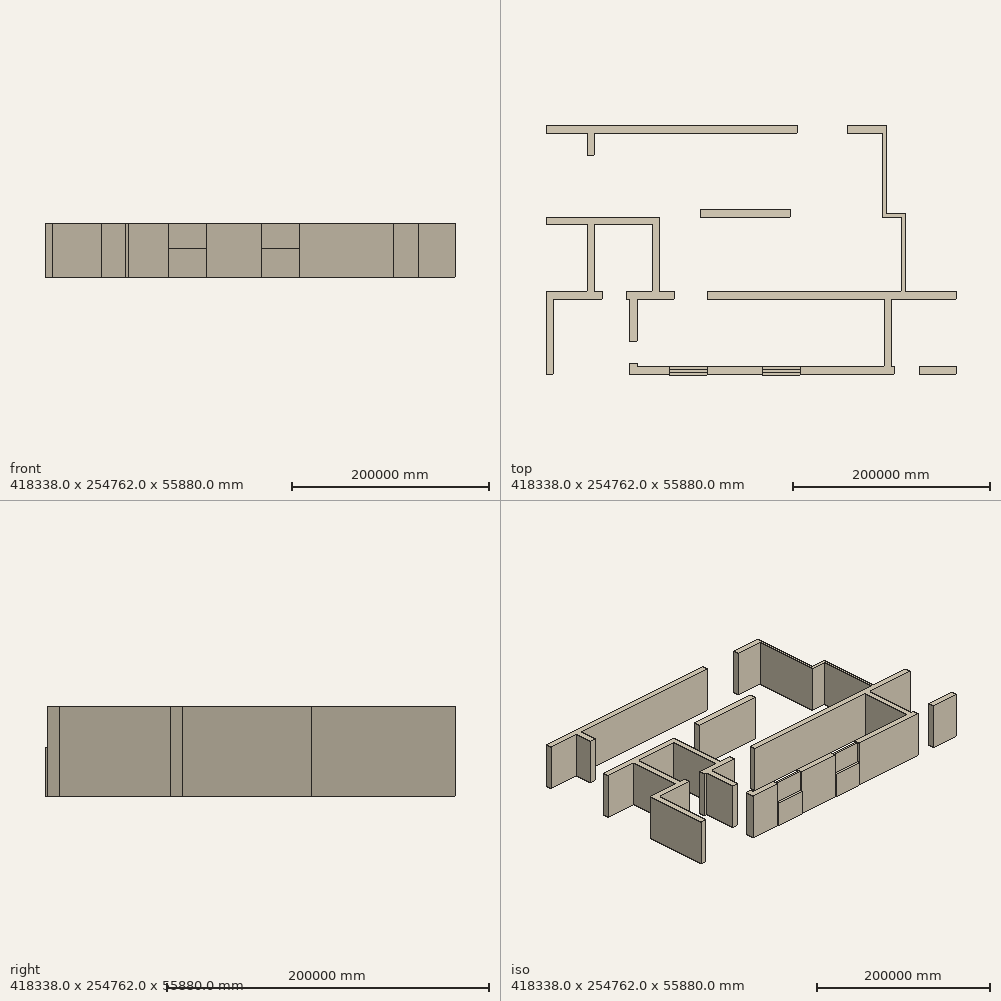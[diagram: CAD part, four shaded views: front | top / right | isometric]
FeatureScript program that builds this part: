
annotation { "Feature Type Name" : "Feature", "Feature Type Description" : "" }
export const myFeature = defineFeature(function(context is Context, id is Id, definition is map)
    precondition{}
    {
        {
            var Q0;
            Q0=qCreatedBy(makeId("Top.planeOp"),FACE);
            var sketch = newSketch(context, id + "F0", { "sketchPlane" : qUnion([Q0])});
            skLineSegment(sketch, "E0", {"start": v(0, 0) * mm, "end": v(115316, 0) * mm});
            skLineSegment(sketch, "E1", {"start": v(115316, 0) * mm, "end": v(115316, -76200) * mm});
            skLineSegment(sketch, "E2", {"start": v(115316, -76200) * mm, "end": v(130810, -76200) * mm});
            skLineSegment(sketch, "E3", {"start": v(130810, -76200) * mm, "end": v(130810, -83820) * mm});
            skLineSegment(sketch, "E4", {"start": v(130810, -83820) * mm, "end": v(92710, -83820) * mm});
            skLineSegment(sketch, "E5", {"start": v(92710, -83820) * mm, "end": v(92710, -127000) * mm});
            skLineSegment(sketch, "E6", {"start": v(92710, -127000) * mm, "end": v(85090, -127000) * mm});
            skLineSegment(sketch, "E7", {"start": v(85090, -127000) * mm, "end": v(85090, -83820) * mm});
            skLineSegment(sketch, "E8", {"start": v(85090, -83820) * mm, "end": v(81280, -83820) * mm});
            skLineSegment(sketch, "E9", {"start": v(81280, -83820) * mm, "end": v(81280, -76200) * mm});
            skLineSegment(sketch, "E10", {"start": v(81280, -76200) * mm, "end": v(107696, -76200) * mm});
            skLineSegment(sketch, "E11", {"start": v(107696, -76200) * mm, "end": v(107696, -7620) * mm});
            skLineSegment(sketch, "E12", {"start": v(107696, -7620) * mm, "end": v(49276, -7620) * mm});
            skLineSegment(sketch, "E13", {"start": v(49276, -7620) * mm, "end": v(49276, -76200) * mm});
            skLineSegment(sketch, "E14", {"start": v(49276, -76200) * mm, "end": v(56896, -76200) * mm});
            skLineSegment(sketch, "E15", {"start": v(56896, -76200) * mm, "end": v(56896, -83820) * mm});
            skLineSegment(sketch, "E16", {"start": v(56896, -83820) * mm, "end": v(7620, -83820) * mm});
            skLineSegment(sketch, "E17", {"start": v(7620, -83820) * mm, "end": v(7620, -160020) * mm});
            skLineSegment(sketch, "E18", {"start": v(7620, -160020) * mm, "end": v(0, -160020) * mm});
            skLineSegment(sketch, "E19", {"start": v(0, -160020) * mm, "end": v(0, -76200) * mm});
            skLineSegment(sketch, "E20", {"start": v(0, -76200) * mm, "end": v(41656, -76200) * mm});
            skLineSegment(sketch, "E21", {"start": v(41656, -76200) * mm, "end": v(41656, -7620) * mm});
            skLineSegment(sketch, "E22", {"start": v(41656, -7620) * mm, "end": v(0, -7620) * mm});
            skLineSegment(sketch, "E23", {"start": v(0, -7620) * mm, "end": v(0, 0) * mm});
            skLineSegment(sketch, "E24", {"start": v(164338, -83820) * mm, "end": v(164338, -76200) * mm});
            skLineSegment(sketch, "E25", {"start": v(164338, -76200) * mm, "end": v(362458, -76200) * mm});
            skLineSegment(sketch, "E26", {"start": v(418338, -76200) * mm, "end": v(418338, -83820) * mm});
            skLineSegment(sketch, "E27", {"start": v(418338, -83820) * mm, "end": v(352298, -83820) * mm});
            skLineSegment(sketch, "E28", {"start": v(352298, -83820) * mm, "end": v(352298, -152400) * mm});
            skLineSegment(sketch, "E29", {"start": v(352298, -152400) * mm, "end": v(355346, -152400) * mm});
            skLineSegment(sketch, "E30", {"start": v(355346, -152400) * mm, "end": v(355346, -160020) * mm});
            skLineSegment(sketch, "E31", {"start": v(355346, -160020) * mm, "end": v(258826, -160020) * mm});
            skLineSegment(sketch, "E32", {"start": v(258826, -160020) * mm, "end": v(258826, -152400) * mm});
            skLineSegment(sketch, "E33", {"start": v(258826, -152400) * mm, "end": v(344678, -152400) * mm});
            skLineSegment(sketch, "E34", {"start": v(344678, -152400) * mm, "end": v(344678, -83820) * mm});
            skLineSegment(sketch, "E35", {"start": v(344678, -83820) * mm, "end": v(164338, -83820) * mm});
            skLineSegment(sketch, "E36", {"start": v(380746, -152400) * mm, "end": v(380746, -160020) * mm});
            skLineSegment(sketch, "E37", {"start": v(380746, -160020) * mm, "end": v(418338, -160020) * mm});
            skLineSegment(sketch, "E38", {"start": v(418338, -160020) * mm, "end": v(418338, -152400) * mm});
            skLineSegment(sketch, "E39", {"start": v(418338, -152400) * mm, "end": v(380746, -152400) * mm});
            skLineSegment(sketch, "E40", {"start": v(85090, -160020) * mm, "end": v(125730, -160020) * mm});
            skLineSegment(sketch, "E41", {"start": v(125730, -160020) * mm, "end": v(125730, -152400) * mm});
            skLineSegment(sketch, "E42", {"start": v(125730, -152400) * mm, "end": v(92710, -152400) * mm});
            skLineSegment(sketch, "E43", {"start": v(92710, -152400) * mm, "end": v(92710, -148844) * mm});
            skLineSegment(sketch, "E44", {"start": v(92710, -148844) * mm, "end": v(85090, -148844) * mm});
            skLineSegment(sketch, "E45", {"start": v(85090, -148844) * mm, "end": v(85090, -160020) * mm});
            skLineSegment(sketch, "E46", {"start": v(164338, -152400) * mm, "end": v(220218, -152400) * mm});
            skLineSegment(sketch, "E47", {"start": v(220218, -152400) * mm, "end": v(220218, -160020) * mm});
            skLineSegment(sketch, "E48", {"start": v(220218, -160020) * mm, "end": v(164338, -160020) * mm});
            skLineSegment(sketch, "E49", {"start": v(164338, -160020) * mm, "end": v(164338, -152400) * mm});
            skLineSegment(sketch, "E50", {"start": v(125730, -152400) * mm, "end": v(164338, -152400) * mm});
            skLineSegment(sketch, "E51", {"start": v(125730, -160020) * mm, "end": v(125730, -161290) * mm});
            skLineSegment(sketch, "E52", {"start": v(125730, -161290) * mm, "end": v(164338, -161290) * mm});
            skLineSegment(sketch, "E53", {"start": v(164338, -161290) * mm, "end": v(164338, -160020) * mm});
            skLineSegment(sketch, "E54", {"start": v(125730, -155575) * mm, "end": v(164338, -155575) * mm});
            skLineSegment(sketch, "E55", {"start": v(164338, -155575) * mm, "end": v(164338, -158115) * mm});
            skLineSegment(sketch, "E56", {"start": v(164338, -158115) * mm, "end": v(125730, -158115) * mm});
            skLineSegment(sketch, "E57", {"start": v(125730, -158115) * mm, "end": v(125730, -155575) * mm});
            skLineSegment(sketch, "E58", {"start": v(220218, -152400) * mm, "end": v(258826, -152400) * mm});
            skLineSegment(sketch, "E59", {"start": v(258826, -160020) * mm, "end": v(258826, -161290) * mm});
            skLineSegment(sketch, "E60", {"start": v(258826, -161290) * mm, "end": v(220218, -161290) * mm});
            skLineSegment(sketch, "E61", {"start": v(220218, -161290) * mm, "end": v(220218, -160020) * mm});
            skLineSegment(sketch, "E62", {"start": v(220218, -155575) * mm, "end": v(258826, -155575) * mm});
            skLineSegment(sketch, "E63", {"start": v(258826, -155575) * mm, "end": v(258826, -158115) * mm});
            skLineSegment(sketch, "E64", {"start": v(258826, -158115) * mm, "end": v(220218, -158115) * mm});
            skLineSegment(sketch, "E65", {"start": v(220218, -158115) * mm, "end": v(220218, -155575) * mm});
            skLineSegment(sketch, "E66", {"start": v(362458, -76200) * mm, "end": v(362458, 0) * mm});
            skLineSegment(sketch, "E67", {"start": v(362458, 0) * mm, "end": v(342646, 0) * mm});
            skLineSegment(sketch, "E68", {"start": v(342646, 0) * mm, "end": v(342646, 85852) * mm});
            skLineSegment(sketch, "E69", {"start": v(342646, 85852) * mm, "end": v(307086, 85852) * mm});
            skLineSegment(sketch, "E70", {"start": v(307086, 85852) * mm, "end": v(307086, 93472) * mm});
            skLineSegment(sketch, "E71", {"start": v(307086, 93472) * mm, "end": v(346456, 93472) * mm});
            skLineSegment(sketch, "E72", {"start": v(346456, 93472) * mm, "end": v(346456, 3810) * mm});
            skLineSegment(sketch, "E73", {"start": v(346456, 3810) * mm, "end": v(366268, 3810) * mm});
            skLineSegment(sketch, "E74", {"start": v(366268, 3810) * mm, "end": v(366268, -76200) * mm});
            skLineSegment(sketch, "E75.trimOffspring", {"start": v(366268, -76200) * mm, "end": v(418338, -76200) * mm});
            skLineSegment(sketch, "E76", {"start": v(248666, 0) * mm, "end": v(157226, 0) * mm});
            skLineSegment(sketch, "E77", {"start": v(157226, 0) * mm, "end": v(157226, 7620) * mm});
            skLineSegment(sketch, "E78", {"start": v(157226, 7620) * mm, "end": v(248666, 7620) * mm});
            skLineSegment(sketch, "E79", {"start": v(248666, 7620) * mm, "end": v(248666, 0) * mm});
            skLineSegment(sketch, "E80", {"start": v(256286, 85852) * mm, "end": v(49276, 85852) * mm});
            skLineSegment(sketch, "E81", {"start": v(49276, 85852) * mm, "end": v(49276, 62992) * mm});
            skLineSegment(sketch, "E82", {"start": v(49276, 62992) * mm, "end": v(41656, 62992) * mm});
            skLineSegment(sketch, "E83", {"start": v(41656, 62992) * mm, "end": v(41656, 85852) * mm});
            skLineSegment(sketch, "E84", {"start": v(41656, 85852) * mm, "end": v(0, 85852) * mm});
            skLineSegment(sketch, "E85", {"start": v(0, 85852) * mm, "end": v(0, 93472) * mm});
            skLineSegment(sketch, "E86", {"start": v(0, 93472) * mm, "end": v(256286, 93472) * mm});
            skLineSegment(sketch, "E87", {"start": v(256286, 93472) * mm, "end": v(256286, 85852) * mm});
            skSolve(sketch);
        }
        {
            var Q0;
            Q0=makeQuery(id+"F0.imprint","IMPRINT",FACE,{"disambiguationData":[TD([[makeQuery(id+"F0.imprint","IMPRINT",EDGE,{"derivedFrom":sQuery(id+"F0.wireOp",EDGE,"E0")}),-1.0]])]});
            var Q1;
            Q1=makeQuery(id+"F0.imprint","IMPRINT",FACE,{"disambiguationData":[TD([[makeQuery(id+"F0.imprint","IMPRINT",EDGE,{"derivedFrom":sQuery(id+"F0.wireOp",EDGE,"E36")}),1.0]])]});
            var Q2;
            Q2=makeQuery(id+"F0.imprint","IMPRINT",FACE,{"disambiguationData":[TD([[makeQuery(id+"F0.imprint","IMPRINT",EDGE,{"derivedFrom":sQuery(id+"F0.wireOp",EDGE,"E76")}),-1.0]])]});
            var Q3;
            Q3=makeQuery(id+"F0.imprint","IMPRINT",FACE,{"disambiguationData":[TD([[makeQuery(id+"F0.imprint","IMPRINT",EDGE,{"derivedFrom":sQuery(id+"F0.wireOp",EDGE,"E80")}),-1.0]])]});
            var Q4;
            Q4=makeQuery(id+"F0.imprint","IMPRINT",FACE,{"disambiguationData":[TD([[makeQuery(id+"F0.imprint","IMPRINT",EDGE,{"derivedFrom":sQuery(id+"F0.wireOp",EDGE,"E24")}),-1.0]])]});
            var Q5;
            {var subQ3=sQuery(id+"F0.wireOp",EDGE,"E40");Q5=makeQuery(id+"F0.imprint","IMPRINT",FACE,{"disambiguationData":[TD([[makeQuery(id+"F0.imprint","IMPRINT",EDGE,{"derivedFrom":subQ3}),1.0]])]});}
            var Q6;
            {var subQ3=sQuery(id+"F0.wireOp",EDGE,"E46");Q6=makeQuery(id+"F0.imprint","IMPRINT",FACE,{"disambiguationData":[TD([[makeQuery(id+"F0.imprint","IMPRINT",EDGE,{"derivedFrom":subQ3}),-1.0]])]});}
            extrude(context, id + "F1", {"entities" : qUnion([Q0, Q1, Q2, Q3, Q4, Q5, Q6]), "depth" : 55880 * mm});
        }
        {
            var Q0;
            {var subQ0=sQuery(id+"F0.wireOp",EDGE,"E51");Q0=makeQuery(id+"F0.imprint","IMPRINT",FACE,{"disambiguationData":[TD([[makeQuery(id+"F0.imprint","IMPRINT",EDGE,{"derivedFrom":subQ0}),1.0]])]});}
            var Q1;
            {var subQ0=sQuery(id+"F0.wireOp",EDGE,"E50");Q1=makeQuery(id+"F0.imprint","IMPRINT",FACE,{"disambiguationData":[TD([[makeQuery(id+"F0.imprint","IMPRINT",EDGE,{"derivedFrom":subQ0}),-1.0]])]});}
            var Q2;
            {var subQ0=sQuery(id+"F0.wireOp",EDGE,"E59");Q2=makeQuery(id+"F0.imprint","IMPRINT",FACE,{"disambiguationData":[TD([[makeQuery(id+"F0.imprint","IMPRINT",EDGE,{"derivedFrom":subQ0}),-1.0]])]});}
            var Q3;
            {var subQ0=sQuery(id+"F0.wireOp",EDGE,"E58");Q3=makeQuery(id+"F0.imprint","IMPRINT",FACE,{"disambiguationData":[TD([[makeQuery(id+"F0.imprint","IMPRINT",EDGE,{"derivedFrom":subQ0}),-1.0]])]});}
            extrude(context, id + "F2", {"entities" : qUnion([Q0, Q1, Q2, Q3]), "depth" : 30480 * mm});
        }
        {
            var Q0;
            Q0=makeQuery(id+"F0.imprint","IMPRINT",FACE,{"disambiguationData":[TD([[makeQuery(id+"F0.imprint","IMPRINT",EDGE,{"derivedFrom":sQuery(id+"F0.wireOp",EDGE,"E54")}),-1.0]])]});
            var Q1;
            Q1=makeQuery(id+"F0.imprint","IMPRINT",FACE,{"disambiguationData":[TD([[makeQuery(id+"F0.imprint","IMPRINT",EDGE,{"derivedFrom":sQuery(id+"F0.wireOp",EDGE,"E62")}),-1.0]])]});
            extrude(context, id + "F3", {"entities" : qUnion([Q0, Q1]), "depth" : 55880 * mm});
        }
    });
